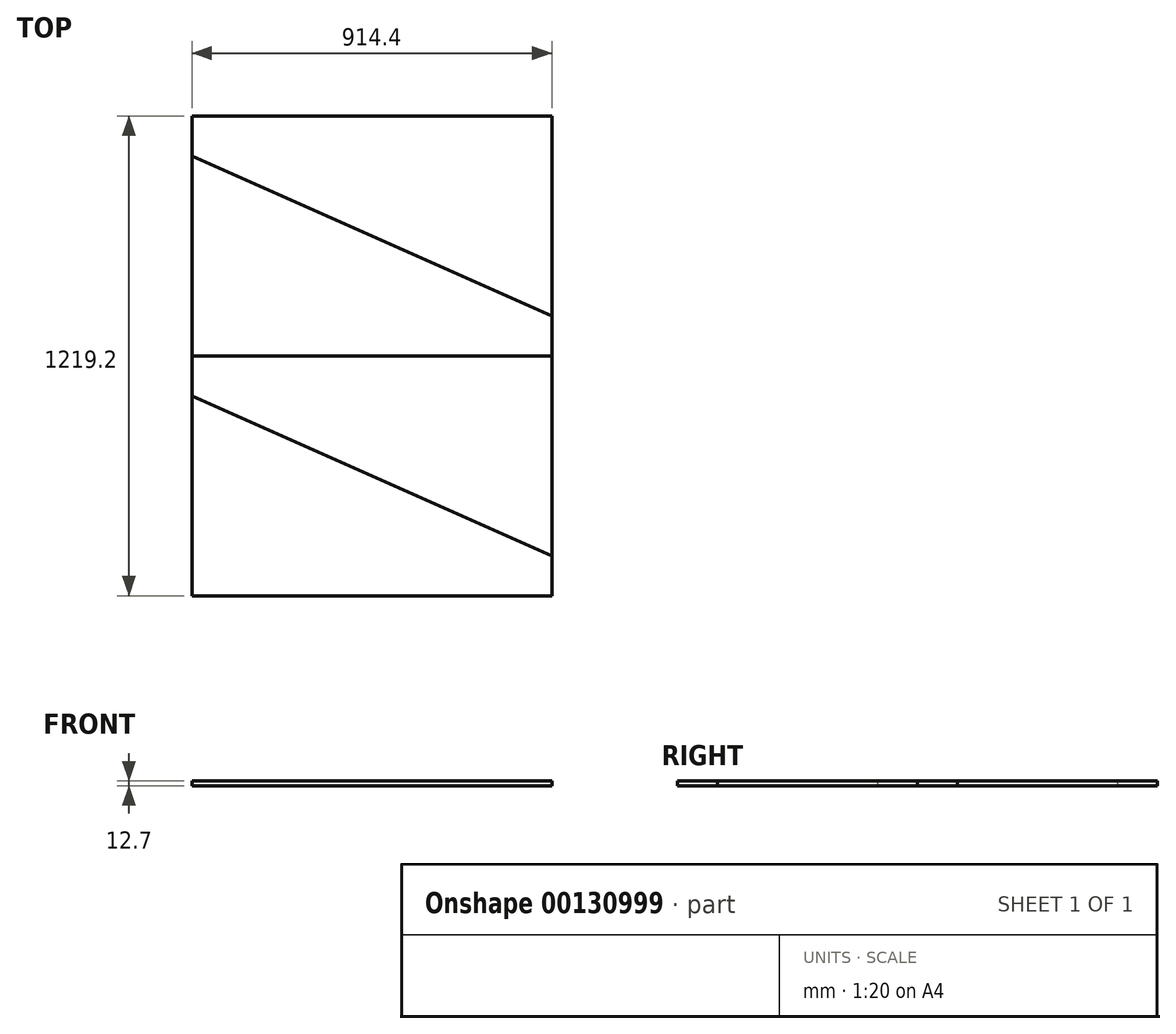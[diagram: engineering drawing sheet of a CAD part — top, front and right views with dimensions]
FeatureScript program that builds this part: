
annotation { "Feature Type Name" : "Feature", "Feature Type Description" : "" }
export const myFeature = defineFeature(function(context is Context, id is Id, definition is map)
    precondition{}
    {
        {
            var Q0;
            Q0=qCreatedBy(makeId("Top.planeOp"),FACE);
            var sketch = newSketch(context, id + "F0", { "sketchPlane" : qUnion([Q0])});
            skLineSegment(sketch, "E0.bottom", {"start": v(-1206.91, 609.6) * mm, "end": v(1231.49, 609.6) * mm});
            skLineSegment(sketch, "E0.top", {"start": v(-1206.91, -609.6) * mm, "end": v(1231.49, -609.6) * mm});
            skLineSegment(sketch, "E0.left", {"start": v(-1206.91, 609.6) * mm, "end": v(-1206.91, -609.6) * mm});
            skLineSegment(sketch, "E0.right", {"start": v(1231.49, 609.6) * mm, "end": v(1231.49, -609.6) * mm});
            skLineSegment(sketch, "E1", {"start": v(-292.51, 609.6) * mm, "end": v(-292.51, -609.6) * mm});
            skLineSegment(sketch, "E2", {"start": v(-1206.91, 0) * mm, "end": v(-292.51, 0) * mm});
            skLineSegment(sketch, "E3", {"start": v(-1206.91, 508) * mm, "end": v(-292.51, 101.6) * mm});
            skLineSegment(sketch, "E4", {"start": v(-1206.91, -101.6) * mm, "end": v(-292.51, -508) * mm});
            skSolve(sketch);
        }
        {
            var Q0;
            {var subQ5=sQuery(id+"F0.wireOp",EDGE,"E3");Q0=makeQuery(id+"F0.imprint","IMPRINT",FACE,{"disambiguationData":[TD([[makeQuery(id+"F0.imprint","IMPRINT",EDGE,{"derivedFrom":subQ5}),1.0]])]});}
            extrude(context, id + "F1", {"entities" : qUnion([Q0]), "depth" : 12.7 * mm});
        }
        {
            var Q0;
            {var subQ0=sQuery(id+"F0.wireOp",EDGE,"E2");Q0=makeQuery(id+"F0.imprint","IMPRINT",FACE,{"disambiguationData":[TD([[makeQuery(id+"F0.imprint","IMPRINT",EDGE,{"derivedFrom":subQ0}),1.0]])]});}
            extrude(context, id + "F2", {"entities" : qUnion([Q0]), "depth" : 12.7 * mm});
        }
        {
            var Q0;
            {var subQ0=sQuery(id+"F0.wireOp",EDGE,"E2");Q0=makeQuery(id+"F0.imprint","IMPRINT",FACE,{"disambiguationData":[TD([[makeQuery(id+"F0.imprint","IMPRINT",EDGE,{"derivedFrom":subQ0}),-1.0]])]});}
            extrude(context, id + "F3", {"entities" : qUnion([Q0]), "depth" : 12.7 * mm});
        }
        {
            var Q0;
            {var subQ5=sQuery(id+"F0.wireOp",EDGE,"E4");Q0=makeQuery(id+"F0.imprint","IMPRINT",FACE,{"disambiguationData":[TD([[makeQuery(id+"F0.imprint","IMPRINT",EDGE,{"derivedFrom":subQ5}),-1.0]])]});}
            extrude(context, id + "F4", {"entities" : qUnion([Q0]), "depth" : 12.7 * mm});
        }
    });
